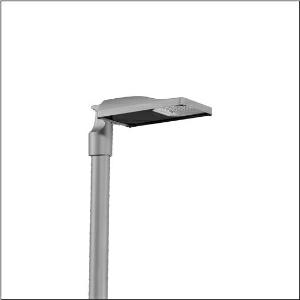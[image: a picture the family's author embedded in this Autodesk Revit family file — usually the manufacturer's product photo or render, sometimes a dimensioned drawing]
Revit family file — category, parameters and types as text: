
# Revit family: streetlight_sl_31_micro___st1_0a_5xh1d71b08da_111b
name_source: partatom
category: Lighting Fixtures
units: mm (PartAtom-declared; Revit-internal decimal feet)

## family parameters
Cut with Voids When Loaded = No
Host = Face
Light Source = No
Part Type = Normal
Room Calculation Point = No
Round Connector Dimension = Use Diameter
Shared = No

## types (1)
- --- (1 x LED, 3800 lm, 35.5 W, 2200K)
    Apparent Load = 36 VA
    CIE Flux Codes = 37 72 97 100 100
    Color Rendering = 70
    Color Temperature = 2200K
    Default Elevation = 1800 mm
    Description = Streetlight SL 31 micro Easy, LST, Desk-Remote mast luminaire for post-top, side-entry; light control with lens of PMMA; light distribution: ST1.0a, direct asymmetric distribution, for standard-compliant lighting for roads and squares; LED: luminous flux: 3.800lm, light colour: 722, colour temperature: 2200K; luminous efficacy: 107lm/W; control: pre-setting: linear dimming characteristic, flexible luminous flux parameterisation, time-dependent luminous flux control, constant luminous flux control, power reduction, intelligent temperature release in ECG and LED module, overheat protection; luminaire housing, of diecast aluminium, SITECO metallic grey (DB 702S), corrosivity category C5 high according to DIN EN ISO 12944; cover of toughened safety glass, transparent, mast flange of diecast aluminium, SITECO metallic grey (DB 702S), spigot size: 76/60mm, mast flange included unmounted; cable length: 6,5m, connection cable pre-assembled; mains connection: 220..240V, AC, 50/60Hz; power consumption (at start of service life): 35,5W / (at end of service life): 37,5W / (with reduced operation 50%): 15,4W; protection rating (complete): IP66; insulation class (complete): insulation class II (safety insulation); impact resistance: IK10; certification: CE, ENEC, ENEC+, VDE, UKCA; permissible operating ambient temperature for outdoor applications: -40..+50°C; packaging unit: 1 piece

Light Distribution: ST1.0a
    Height = 76 mm
    Lamp = 1 x LED
    Lamp Light Flux = 3800 lm
    Lamp Power = 35.5 W
    Lamp count = 1
    Length = 467 mm
    Luminous efficacy = 107 lm/W
    Manufacturer = Siteco
    ModVariant = No
    Model = 5XH1D71B08DA
    Mounting Place = Pole
    Mounting Type = Pole top
    Number of Poles = 1
    OnlyDefault = Yes
    Power Factor = 1
    Product Name = Streetlight SL 31 micro | ST1.0a
    Product group = mast luminaire | pylon top
    ProductGroupID = 6100
    Protection Class = Protection class II
    Protection Degree = IP 66
    RLX_Detail_Level = 1
    RLX_Emergency_Light_Flux = 0 lm
    RLX_Emergency_Type = 0
    RLX_Emergency_Type_DB = No
    RlxData = <blob elided: 23197 chars, md5=edbdf003>
    Socket = socket
    Standby Power = 0 W
    System Light Flux = 3800 lm
    System Power = 36 W
    Type Comments = factory setting: luminous flux: 100 % | dim-lin: 254 | 700 mA
    Type Image = l_1300309.jpg
    URL = http://relux.com
    VarID = @adj_011155
    Voltage = 0 V
    Weight = 0.00 kg
    Width = 265 mm

## geometry (parser evidence)
native form markers: Blend x4, Sweep x10
no freeform markers — native parametric forms only
